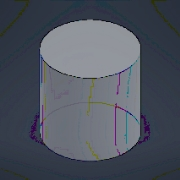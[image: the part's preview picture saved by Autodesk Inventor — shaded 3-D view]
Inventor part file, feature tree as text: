
AUTODESK INVENTOR PART (.ipt)
format: ipt  version: 2025.3 (Build 293356000, 356)  size: 129,536 bytes
history: native  units: mm
features: extrude x1, sketch x1
ambient origin geometry x8: Origin, YZ Plane, XZ Plane, XY Plane, X Axis, Y Axis, Z Axis, Center Point
bodies: Solid1 (feature_tree)
feature tree (2):
  extrude  "Extrusion1"  [1 undecoded]
  sketch  "Sketch1"  dims[d1=240.0mm d2=0.0mm]
note: 1 required parameter value undecoded (feature->parameter linkage not recoverable at this tier; creation-order binding heuristic only, values carry confidence <= 0.55)
